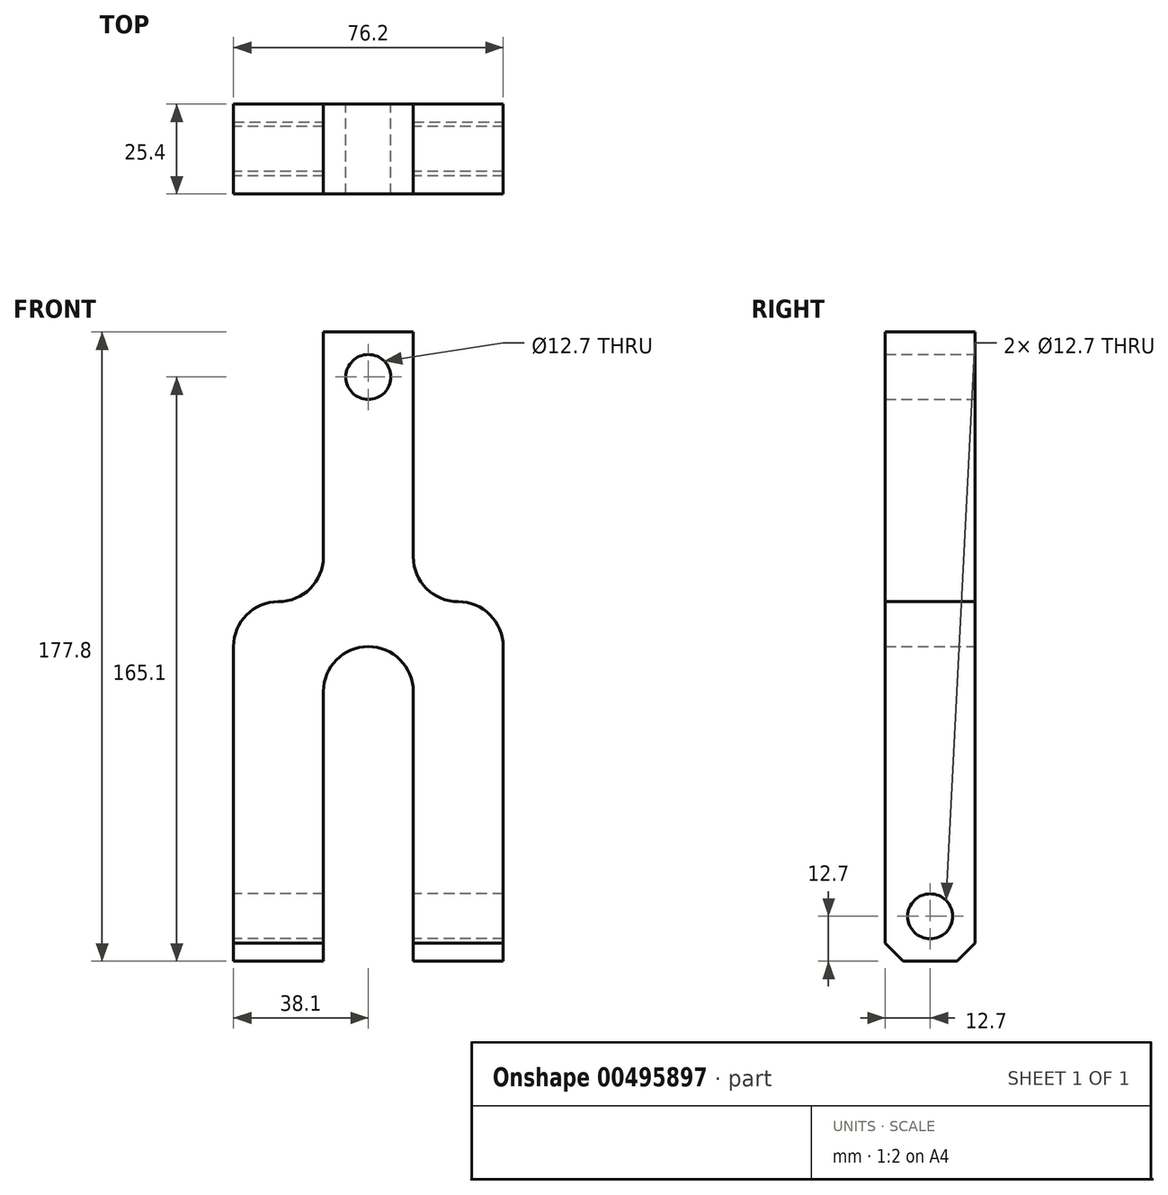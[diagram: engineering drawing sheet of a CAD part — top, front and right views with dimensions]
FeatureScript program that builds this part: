
annotation { "Feature Type Name" : "Feature", "Feature Type Description" : "" }
export const myFeature = defineFeature(function(context is Context, id is Id, definition is map)
    precondition{}
    {
        {
            var Q0;
            Q0=qCreatedBy(makeId("Front.planeOp"),FACE);
            var sketch = newSketch(context, id + "F0", { "sketchPlane" : qUnion([Q0])});
            skLineSegment(sketch, "E0.bottom", {"start": v(-12.7, 53.44) * mm, "end": v(12.7, 53.44) * mm});
            skLineSegment(sketch, "E0.left", {"start": v(-12.7, 53.44) * mm, "end": v(-12.7, -10.06) * mm});
            skLineSegment(sketch, "E0.right", {"start": v(12.7, 53.44) * mm, "end": v(12.7, -10.06) * mm});
            skLineSegment(sketch, "E1", {"start": v(-25.4, -22.76) * mm, "end": v(-25.4, -22.76) * mm});
            skLineSegment(sketch, "E2", {"start": v(25.4, -22.76) * mm, "end": v(25.4, -22.76) * mm});
            skLineSegment(sketch, "E3", {"start": v(-38.1, -35.46) * mm, "end": v(-38.1, -124.36) * mm});
            skLineSegment(sketch, "E4", {"start": v(38.1, -124.36) * mm, "end": v(12.7, -124.36) * mm});
            skLineSegment(sketch, "E5", {"start": v(-38.1, -124.36) * mm, "end": v(-12.7, -124.36) * mm});
            skLineSegment(sketch, "E6", {"start": v(-12.7, -124.36) * mm, "end": v(-12.7, -48.16) * mm});
            skLineSegment(sketch, "E7", {"start": v(12.7, -124.36) * mm, "end": v(12.7, -48.16) * mm});
            skLineSegment(sketch, "E8", {"start": v(38.1, -124.36) * mm, "end": v(38.1, -35.46) * mm});
            skArc(sketch, "E9", {"start": v(12.7, -48.16) * mm, "mid": v(0, -35.46) * mm, "end": v(-12.7, -48.16) * mm});
            skCircle(sketch, "E10", {"center": v(0, 40.74) * mm, "radius": 6.35 * mm});
            skPoint(sketch, "E11.visualSharp", {"position": v(-38.1, -22.76) * mm});
            skArc(sketch, "E11.filletArc", {"start": v(-25.4, -22.76) * mm, "mid": v(-34.38, -26.48) * mm, "end": v(-38.1, -35.46) * mm});
            skPoint(sketch, "E12.visualSharp", {"position": v(38.1, -22.76) * mm});
            skArc(sketch, "E12.filletArc", {"start": v(38.1, -35.46) * mm, "mid": v(34.38, -26.48) * mm, "end": v(25.4, -22.76) * mm});
            skPoint(sketch, "E13.visualSharp", {"position": v(-12.7, -22.76) * mm});
            skArc(sketch, "E13.filletArc", {"start": v(-25.4, -22.76) * mm, "mid": v(-16.42, -19.04) * mm, "end": v(-12.7, -10.06) * mm});
            skPoint(sketch, "E14.visualSharp", {"position": v(12.7, -22.76) * mm});
            skArc(sketch, "E14.filletArc", {"start": v(12.7, -10.06) * mm, "mid": v(16.42, -19.04) * mm, "end": v(25.4, -22.76) * mm});
            skSolve(sketch);
        }
        {
            var Q0;
            Q0 = qSketchRegion(id + "F0", true);
            extrude(context, id + "F1", {"entities" : qUnion([Q0]), "endBound" : BoundingType.SYMMETRIC, "depth" : 25.4 * mm});
        }
        {
            var Q0;
            Q0=makeQuery(id+"F1.opExtrude","SWEPT_FACE",FACE,{"disambiguationData":[OSD([sQuery(id+"F0.wireOp",EDGE,"E3")])]});
            var sketch = newSketch(context, id + "F2", { "sketchPlane" : qUnion([Q0])});
            skCircle(sketch, "E15", {"center": v(0, -111.66) * mm, "radius": 6.35 * mm});
            skSolve(sketch);
        }
        {
            var Q0;
            Q0=makeQuery(id+"F2.imprint","IMPRINT",FACE,{"disambiguationData":[TD([[makeQuery(id+"F2.imprint","IMPRINT",EDGE,{"derivedFrom":sQuery(id+"F2.wireOp",EDGE,"E15")}),1.0]])]});
            extrude(context, id + "F3", {"entities" : qUnion([Q0]), "operationType" : NewBodyOperationType.REMOVE, "oppositeDirection" : true, "depth" : 76.2 * mm, "offsetDistance" : 25.4 * mm});
        }
        {
            var Q0;
            Q0=makeQuery(id+"F1.opExtrude","CAP_EDGE",EDGE,{"disambiguationData":[OSD([sQuery(id+"F0.wireOp",EDGE,"E5")])],"isStart":false});
            var Q1;
            Q1=makeQuery(id+"F1.opExtrude","CAP_EDGE",EDGE,{"disambiguationData":[OSD([sQuery(id+"F0.wireOp",EDGE,"E4")])],"isStart":false});
            var Q2;
            Q2=makeQuery(id+"F1.opExtrude","CAP_EDGE",EDGE,{"disambiguationData":[OSD([sQuery(id+"F0.wireOp",EDGE,"E4")])],"isStart":true});
            var Q3;
            Q3=makeQuery(id+"F1.opExtrude","CAP_EDGE",EDGE,{"disambiguationData":[OSD([sQuery(id+"F0.wireOp",EDGE,"E5")])],"isStart":true});
            chamfer(context, id + "F4", {"entities" : qUnion([Q0, Q1, Q2, Q3]), "width" : 5.08 * mm, "tangentPropagation" : true});
        }
    });
